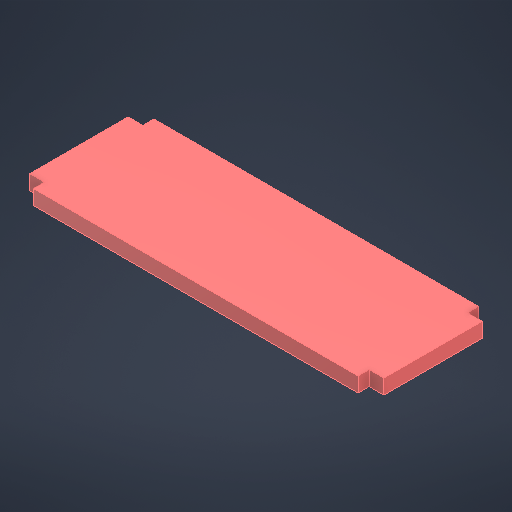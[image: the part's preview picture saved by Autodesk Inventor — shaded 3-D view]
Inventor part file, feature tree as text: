
AUTODESK INVENTOR PART (.ipt)
format: ipt  version: 2025.3 (Build 293356030, 356C)  size: 227,840 bytes
history: native  units: mm
features: other x1, extrude x1, sketch x1
ambient origin geometry x8: Origin, YZ Plane, XZ Plane, XY Plane, X Axis, Y Axis, Z Axis, Center Point
bodies: Body1 (feature_tree)
feature tree (3):
  other  "實體1"
  extrude  "擠出1"  Depth=66.0mm
  sketch  "草圖1"
